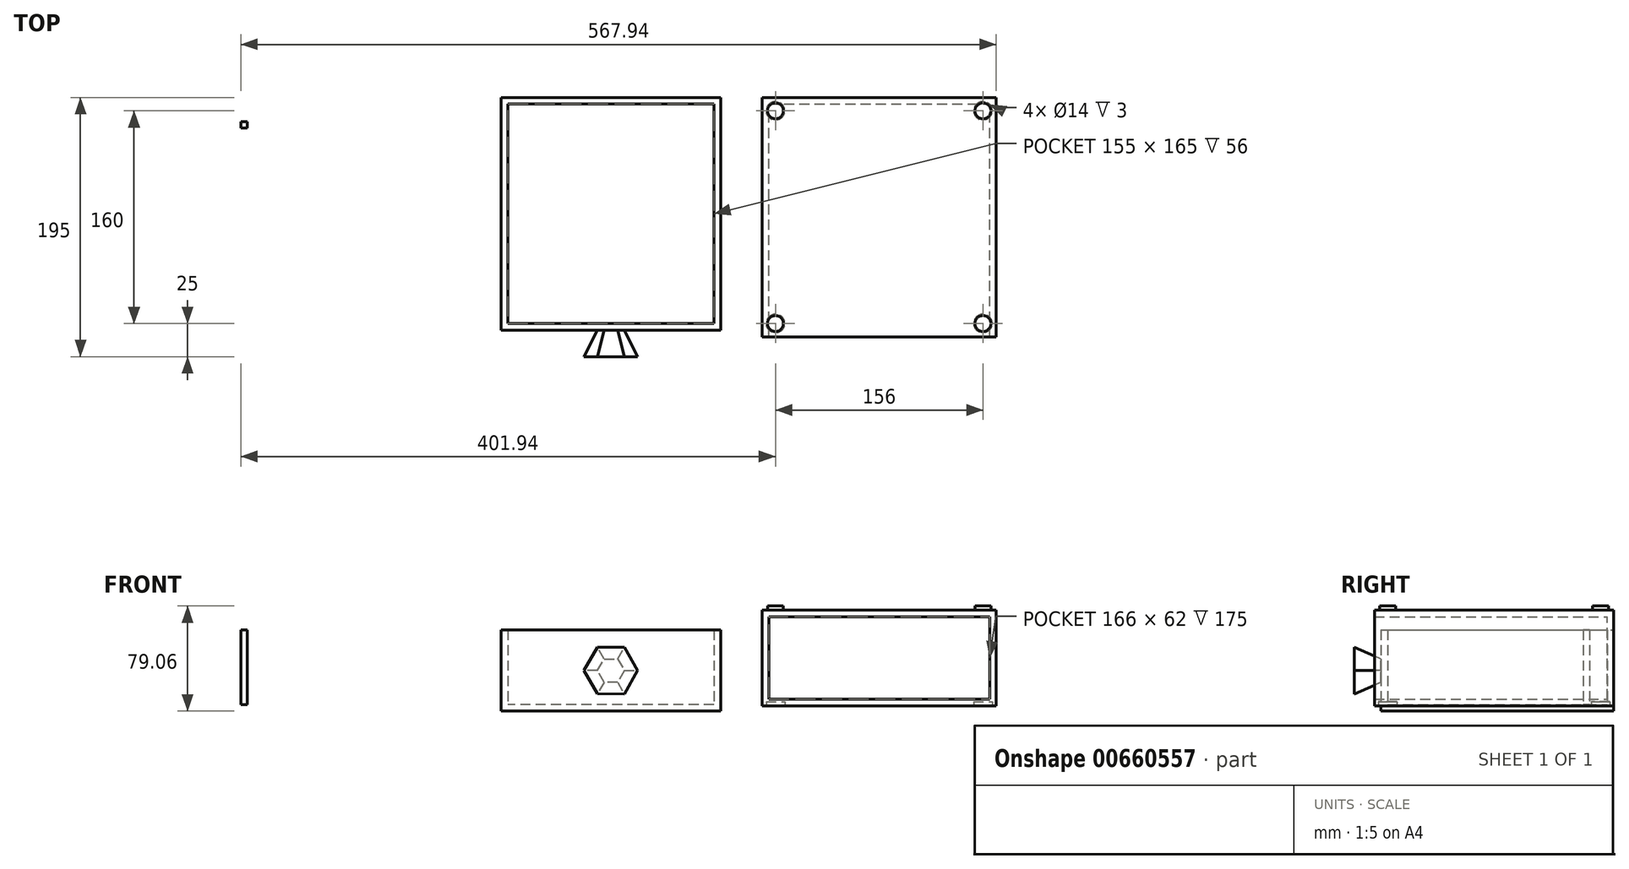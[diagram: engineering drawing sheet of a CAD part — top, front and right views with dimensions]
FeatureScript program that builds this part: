
annotation { "Feature Type Name" : "Feature", "Feature Type Description" : "" }
export const myFeature = defineFeature(function(context is Context, id is Id, definition is map)
    precondition{}
    {
        {
            var Q0;
            Q0=qCreatedBy(makeId("Front.planeOp"),FACE);
            var sketch = newSketch(context, id + "F0", { "sketchPlane" : qUnion([Q0])});
            skLineSegment(sketch, "E0.bottom", {"start": v(-21.74, -12.57) * mm, "end": v(144.26, -12.57) * mm});
            skLineSegment(sketch, "E0.top", {"start": v(-21.74, 49.43) * mm, "end": v(144.26, 49.43) * mm});
            skLineSegment(sketch, "E0.left", {"start": v(-21.74, -12.57) * mm, "end": v(-21.74, 49.43) * mm});
            skLineSegment(sketch, "E0.right", {"start": v(144.26, -12.57) * mm, "end": v(144.26, 49.43) * mm});
            skLineSegment(sketch, "E1.bottom", {"start": v(-26.74, -17.57) * mm, "end": v(149.26, -17.57) * mm});
            skLineSegment(sketch, "E1.top", {"start": v(-26.74, 54.43) * mm, "end": v(149.26, 54.43) * mm});
            skLineSegment(sketch, "E1.left", {"start": v(-26.74, -17.57) * mm, "end": v(-26.74, 54.43) * mm});
            skLineSegment(sketch, "E1.right", {"start": v(149.26, -17.57) * mm, "end": v(149.26, 54.43) * mm});
            skSolve(sketch);
        }
        {
            var Q0;
            Q0=makeQuery(id+"F0.imprint","IMPRINT",FACE,{"disambiguationData":[TD([[makeQuery(id+"F0.imprint","IMPRINT",EDGE,{"derivedFrom":sQuery(id+"F0.wireOp",EDGE,"E0.bottom")}),1.0]])]});
            extrude(context, id + "F1", {"entities" : qUnion([Q0]), "depth" : 5 * mm, "offsetDistance" : 25 * mm});
        }
        {
            var Q0;
            Q0=makeQuery(id+"F0.imprint","IMPRINT",FACE,{"disambiguationData":[TD([[makeQuery(id+"F0.imprint","IMPRINT",EDGE,{"derivedFrom":sQuery(id+"F0.wireOp",EDGE,"E0.bottom")}),-1.0]])]});
            extrude(context, id + "F2", {"entities" : qUnion([Q0]), "operationType" : NewBodyOperationType.ADD, "depth" : 180 * mm, "offsetDistance" : 25 * mm});
        }
        {
            var Q0;
            Q0=qCreatedBy(makeId("Front.planeOp"),FACE);
            var sketch = newSketch(context, id + "F3", { "sketchPlane" : qUnion([Q0])});
            skLineSegment(sketch, "E2.bottom", {"start": v(-57.99, 39.37) * mm, "end": v(-222.99, 39.37) * mm});
            skLineSegment(sketch, "E2.top", {"start": v(-57.99, -21.63) * mm, "end": v(-222.99, -21.63) * mm});
            skLineSegment(sketch, "E2.left", {"start": v(-57.99, 39.37) * mm, "end": v(-57.99, -21.63) * mm});
            skLineSegment(sketch, "E2.right", {"start": v(-222.99, 39.37) * mm, "end": v(-222.99, -21.63) * mm});
            skSolve(sketch);
        }
        {
            var Q0;
            Q0=qSketchRegion(id+"F3",true);
            var Q1;
            Q1=makeQuery(id+"F3.imprint","IMPRINT",FACE,{"disambiguationData":[TD([[makeQuery(id+"F3.imprint","IMPRINT",EDGE,{"derivedFrom":sQuery(id+"F3.wireOp",EDGE,"E2.bottom")}),1.0]])]});
            extrude(context, id + "F4", {"entities" : qUnion([Q0, Q1]), "depth" : 175 * mm, "offsetDistance" : 25 * mm});
        }
        {
            var Q0;
            Q0=makeQuery(id+"F4.opExtrude","SWEPT_FACE",FACE,{"disambiguationData":[OSD([sQuery(id+"F3.wireOp",EDGE,"E2.bottom")])]});
            shell(context, id + "F5", {"entities" : qUnion([Q0]), "thickness" : 5 * mm});
        }
        {
            var Q0;
            Q0=makeQuery(id+"F4.opExtrude","CAP_FACE",FACE,{"disambiguationData":[OSD([sQuery(id+"F3.wireOp",EDGE,"E2.bottom"),sQuery(id+"F3.wireOp",EDGE,"E2.top"),sQuery(id+"F3.wireOp",EDGE,"E2.left"),sQuery(id+"F3.wireOp",EDGE,"E2.right")])],"isStart":false});
            var sketch = newSketch(context, id + "F6", { "sketchPlane" : qUnion([Q0])});
            skLineSegment(sketch, "E3", {"start": v(-222.99, 25.49) * mm, "end": v(-57.99, 25.49) * mm, "construction": true});
            skLineSegment(sketch, "E4", {"start": v(-146.55, 39.37) * mm, "end": v(-146.55, -21.63) * mm, "construction": true});
            skPoint(sketch, "E5", {"position": v(-146.55, 8.87) * mm});
            skPoint(sketch, "E6", {"position": v(-140.49, 25.49) * mm});
            skPoint(sketch, "E7.middle", {"position": v(-140.49, 8.87) * mm});
            skCircle(sketch, "E8.cCircle", {"center": v(-140.49, 8.87) * mm, "radius": 8.75 * mm, "construction": true});
            skLineSegment(sketch, "E8.0", {"start": v(-135.42, 17.61) * mm, "end": v(-130.38, 8.85) * mm});
            skLineSegment(sketch, "E8.1", {"start": v(-130.38, 8.85) * mm, "end": v(-135.46, 0.11) * mm});
            skLineSegment(sketch, "E8.2", {"start": v(-135.46, 0.11) * mm, "end": v(-145.56, 0.13) * mm});
            skLineSegment(sketch, "E8.3", {"start": v(-145.56, 0.13) * mm, "end": v(-150.6, 8.9) * mm});
            skLineSegment(sketch, "E8.4", {"start": v(-150.6, 8.9) * mm, "end": v(-145.52, 17.63) * mm});
            skLineSegment(sketch, "E8.5", {"start": v(-145.52, 17.63) * mm, "end": v(-135.42, 17.61) * mm});
            skPoint(sketch, "E8.0.midPoint", {"position": v(-132.9, 13.23) * mm});
            skSolve(sketch);
        }
        {
            var Q0;
            Q0=makeQuery(id+"F6.imprint","IMPRINT",FACE,{"disambiguationData":[TD([[makeQuery(id+"F6.imprint","IMPRINT",EDGE,{"derivedFrom":sQuery(id+"F6.wireOp",EDGE,"E8.0")}),1.0]])]});
            cPlane(context, id + "F7", {"entities" : qUnion([Q0]), "cplaneType" : CPlaneType.OFFSET, "offset" : 20 * mm, "width" : 150 * mm, "height" : 150 * mm});
        }
        {
            var Q0;
            Q0=qCreatedBy(id+"F7.planeOp",FACE);
            var sketch = newSketch(context, id + "F8", { "sketchPlane" : qUnion([Q0])});
            skCircle(sketch, "E9.cCircle", {"center": v(-140.49, 8.87) * mm, "radius": 17.5 * mm, "construction": true});
            skLineSegment(sketch, "E9.0", {"start": v(-130.34, 26.35) * mm, "end": v(-120.28, 8.83) * mm});
            skLineSegment(sketch, "E9.1", {"start": v(-120.28, 8.83) * mm, "end": v(-130.42, -8.65) * mm});
            skLineSegment(sketch, "E9.2", {"start": v(-130.42, -8.65) * mm, "end": v(-150.63, -8.6) * mm});
            skLineSegment(sketch, "E9.3", {"start": v(-150.63, -8.6) * mm, "end": v(-160.7, 8.92) * mm});
            skLineSegment(sketch, "E9.4", {"start": v(-160.7, 8.92) * mm, "end": v(-150.55, 26.4) * mm});
            skLineSegment(sketch, "E9.5", {"start": v(-150.55, 26.4) * mm, "end": v(-130.34, 26.35) * mm});
            skPoint(sketch, "E9.0.midPoint", {"position": v(-125.31, 17.59) * mm});
            skSolve(sketch);
        }
        {
            var Q1;
            Q1=makeQuery(id+"F6.imprint","IMPRINT",FACE,{"disambiguationData":[TD([[makeQuery(id+"F6.imprint","IMPRINT",EDGE,{"derivedFrom":sQuery(id+"F6.wireOp",EDGE,"E8.0")}),-1.0]])]});
            var Q2;
            Q2=makeQuery(id+"F8.imprint","IMPRINT",FACE,{"disambiguationData":[TD([[makeQuery(id+"F8.imprint","IMPRINT",EDGE,{"derivedFrom":sQuery(id+"F8.wireOp",EDGE,"E9.0")}),-1.0]])]});
            loft(context, id + "F9", {"operationType" : NewBodyOperationType.ADD, "sheetProfilesArray" : [{ "sheetProfileEntities" : qUnion([Q1]) }, { "sheetProfileEntities" : qUnion([Q2]) }]});
        }
        {
            var Q0;
            Q0=makeQuery(id+"F2.opExtrude","SWEPT_FACE",FACE,{"disambiguationData":[OSD([sQuery(id+"F0.wireOp",EDGE,"E1.bottom")])]});
            var sketch = newSketch(context, id + "F10", { "sketchPlane" : qUnion([Q0])});
            skLineSegment(sketch, "E10", {"start": v(-26.74, 170) * mm, "end": v(149.26, 170) * mm, "construction": true});
            skLineSegment(sketch, "E11", {"start": v(-16.74, 180) * mm, "end": v(-16.74, 0) * mm, "construction": true});
            skLineSegment(sketch, "E12", {"start": v(139.26, 180) * mm, "end": v(139.26, 0) * mm, "construction": true});
            skLineSegment(sketch, "E13", {"start": v(-26.74, 10) * mm, "end": v(149.26, 10) * mm, "construction": true});
            skCircle(sketch, "E14", {"center": v(-16.74, 170) * mm, "radius": 6 * mm});
            skCircle(sketch, "E15", {"center": v(139.26, 170) * mm, "radius": 6 * mm});
            skCircle(sketch, "E16", {"center": v(139.26, 10) * mm, "radius": 6 * mm});
            skCircle(sketch, "E17", {"center": v(-16.74, 10) * mm, "radius": 6 * mm});
            skCircle(sketch, "E18", {"center": v(-16.74, 170) * mm, "radius": 7 * mm});
            skCircle(sketch, "E19", {"center": v(139.26, 170) * mm, "radius": 7 * mm});
            skCircle(sketch, "E20", {"center": v(139.26, 10) * mm, "radius": 7 * mm});
            skCircle(sketch, "E21", {"center": v(-16.74, 10) * mm, "radius": 7 * mm});
            skSolve(sketch);
        }
        {
            var Q0;
            Q0=makeQuery(id+"F10.imprint","IMPRINT",FACE,{"disambiguationData":[TD([[makeQuery(id+"F10.imprint","IMPRINT",EDGE,{"derivedFrom":sQuery(id+"F10.wireOp",EDGE,"E14")}),1.0]])]});
            var Q1;
            Q1=makeQuery(id+"F10.imprint","IMPRINT",FACE,{"disambiguationData":[TD([[makeQuery(id+"F10.imprint","IMPRINT",EDGE,{"derivedFrom":sQuery(id+"F10.wireOp",EDGE,"E15")}),1.0]])]});
            var Q2;
            Q2=makeQuery(id+"F10.imprint","IMPRINT",FACE,{"disambiguationData":[TD([[makeQuery(id+"F10.imprint","IMPRINT",EDGE,{"derivedFrom":sQuery(id+"F10.wireOp",EDGE,"E16")}),1.0]])]});
            var Q3;
            Q3=makeQuery(id+"F10.imprint","IMPRINT",FACE,{"disambiguationData":[TD([[makeQuery(id+"F10.imprint","IMPRINT",EDGE,{"derivedFrom":sQuery(id+"F10.wireOp",EDGE,"E17")}),1.0]])]});
            extrude(context, id + "F11", {"entities" : qUnion([Q0, Q1, Q2, Q3]), "operationType" : NewBodyOperationType.ADD, "oppositeDirection" : true, "depth" : 75 * mm, "offsetDistance" : 25 * mm});
        }
        {
            var Q0;
            Q0=qSketchRegion(id+"F10",true);
            extrude(context, id + "F12", {"entities" : qUnion([Q0]), "operationType" : NewBodyOperationType.REMOVE, "oppositeDirection" : true, "depth" : 3 * mm, "offsetDistance" : 25 * mm});
        }
        {
            var Q0;
            Q0=makeQuery(id+"F0.imprint","IMPRINT",FACE,{"disambiguationData":[TD([[makeQuery(id+"F0.imprint","IMPRINT",EDGE,{"derivedFrom":sQuery(id+"F0.wireOp",EDGE,"E0.bottom")}),1.0]])]});
            extrude(context, id + "F13", {"entities" : qUnion([Q0]), "operationType" : NewBodyOperationType.REMOVE, "depth" : 314 * mm, "offsetDistance" : 25 * mm});
        }
        {
            var Q0;
            Q0=makeQuery(id+"F0.imprint","IMPRINT",FACE,{"disambiguationData":[TD([[makeQuery(id+"F0.imprint","IMPRINT",EDGE,{"derivedFrom":sQuery(id+"F0.wireOp",EDGE,"E0.bottom")}),1.0]])]});
            extrude(context, id + "F14", {"entities" : qUnion([Q0]), "operationType" : NewBodyOperationType.ADD, "depth" : 5 * mm, "offsetDistance" : 25 * mm});
        }
        {
            var Q0;
            Q0=makeQuery(id+"F5.opShell","OFFSET_FACE",FACE,{"disambiguationData":[OSD([sQuery(id+"F3.wireOp",EDGE,"E2.top")])]});
            var sketch = newSketch(context, id + "F15", { "sketchPlane" : qUnion([Q0])});
            skLineSegment(sketch, "E22", {"start": v(-208.24, -5) * mm, "end": v(-208.24, -170) * mm, "construction": true});
            skLineSegment(sketch, "E23", {"start": v(-217.99, -154) * mm, "end": v(-62.99, -154) * mm, "construction": true});
            skLineSegment(sketch, "E24.bottom", {"start": v(-493.68, 61.88) * mm, "end": v(-338.68, 61.88) * mm});
            skLineSegment(sketch, "E24.top", {"start": v(-493.68, -103.12) * mm, "end": v(-338.68, -103.12) * mm});
            skLineSegment(sketch, "E24.left", {"start": v(-493.68, 61.88) * mm, "end": v(-493.68, -103.12) * mm});
            skLineSegment(sketch, "E24.right", {"start": v(-338.68, 61.88) * mm, "end": v(-338.68, -103.12) * mm});
            skLineSegment(sketch, "E25.bottom", {"start": v(-418.68, 61.88) * mm, "end": v(-413.68, 61.88) * mm});
            skLineSegment(sketch, "E25.top", {"start": v(-418.68, -103.12) * mm, "end": v(-413.68, -103.12) * mm});
            skLineSegment(sketch, "E25.left", {"start": v(-418.68, 61.88) * mm, "end": v(-418.68, -103.12) * mm});
            skLineSegment(sketch, "E25.right", {"start": v(-413.68, 61.88) * mm, "end": v(-413.68, -103.12) * mm});
            skPoint(sketch, "E26", {"position": v(-416.18, 61.88) * mm});
            skPoint(sketch, "E27", {"position": v(-493.68, -20.62) * mm});
            skLineSegment(sketch, "E28.bottom", {"start": v(-493.68, -18.12) * mm, "end": v(-338.68, -18.12) * mm});
            skLineSegment(sketch, "E28.top", {"start": v(-493.68, -23.12) * mm, "end": v(-338.68, -23.12) * mm});
            skLineSegment(sketch, "E28.left", {"start": v(-493.68, -18.12) * mm, "end": v(-493.68, -23.12) * mm});
            skLineSegment(sketch, "E28.right", {"start": v(-338.68, -18.12) * mm, "end": v(-338.68, -23.12) * mm});
            skSolve(sketch);
        }
        {
            var Q0;
            {var subQ0=sQuery(id+"F15.wireOp",EDGE,"E25.bottom");Q0=makeQuery(id+"F15.imprint","IMPRINT",FACE,{"disambiguationData":[TD([[makeQuery(id+"F15.imprint","IMPRINT",EDGE,{"derivedFrom":subQ0}),-1.0]])]});}
            var Q1;
            {var subQ5=sQuery(id+"F15.wireOp",EDGE,"E28.left");Q1=makeQuery(id+"F15.imprint","IMPRINT",FACE,{"disambiguationData":[TD([[makeQuery(id+"F15.imprint","IMPRINT",EDGE,{"derivedFrom":subQ5}),1.0]])]});}
            var Q2;
            {var subQ0=sQuery(id+"F15.wireOp",EDGE,"E28.bottom");var subQ1=sQuery(id+"F15.wireOp",EDGE,"E25.left");var subQ2=makeQuery(id+"F15.imprint","INTERSECT",VERTEX,{"derivedFrom":[subQ1,subQ0]});Q2=makeQuery(id+"F15.imprint","IMPRINT",FACE,{"disambiguationData":[TD([[makeQuery(id+"F15.imprint","IMPRINT",EDGE,{"disambiguationData":[TD([[subQ2,-1.0]])],"derivedFrom":subQ1}),1.0]])]});}
            var Q3;
            {var subQ5=sQuery(id+"F15.wireOp",EDGE,"E28.right");Q3=makeQuery(id+"F15.imprint","IMPRINT",FACE,{"disambiguationData":[TD([[makeQuery(id+"F15.imprint","IMPRINT",EDGE,{"derivedFrom":subQ5}),-1.0]])]});}
            var Q4;
            {var subQ0=sQuery(id+"F15.wireOp",EDGE,"E25.top");Q4=makeQuery(id+"F15.imprint","IMPRINT",FACE,{"disambiguationData":[TD([[makeQuery(id+"F15.imprint","IMPRINT",EDGE,{"derivedFrom":subQ0}),1.0]])]});}
            extrude(context, id + "F16", {"entities" : qUnion([Q0, Q1, Q2, Q3, Q4]), "depth" : 56 * mm, "offsetDistance" : 25 * mm});
        }
        {
            var Q0;
            Q0=makeQuery(id+"F10.imprint","IMPRINT",FACE,{"disambiguationData":[TD([[makeQuery(id+"F10.imprint","IMPRINT",EDGE,{"derivedFrom":sQuery(id+"F10.wireOp",EDGE,"E17")}),1.0]])]});
            var Q1;
            Q1=makeQuery(id+"F10.imprint","IMPRINT",FACE,{"disambiguationData":[TD([[makeQuery(id+"F10.imprint","IMPRINT",EDGE,{"derivedFrom":sQuery(id+"F10.wireOp",EDGE,"E16")}),1.0]])]});
            var Q2;
            Q2=makeQuery(id+"F10.imprint","IMPRINT",FACE,{"disambiguationData":[TD([[makeQuery(id+"F10.imprint","IMPRINT",EDGE,{"derivedFrom":sQuery(id+"F10.wireOp",EDGE,"E15")}),1.0]])]});
            var Q3;
            Q3=makeQuery(id+"F10.imprint","IMPRINT",FACE,{"disambiguationData":[TD([[makeQuery(id+"F10.imprint","IMPRINT",EDGE,{"derivedFrom":sQuery(id+"F10.wireOp",EDGE,"E14")}),1.0]])]});
            extrude(context, id + "F17", {"entities" : qUnion([Q0, Q1, Q2, Q3]), "operationType" : NewBodyOperationType.REMOVE, "oppositeDirection" : true, "depth" : 3 * mm, "offsetDistance" : 25 * mm, "hasDraft" : true, "draftAngle" : 3 * degree});
        }
    });
